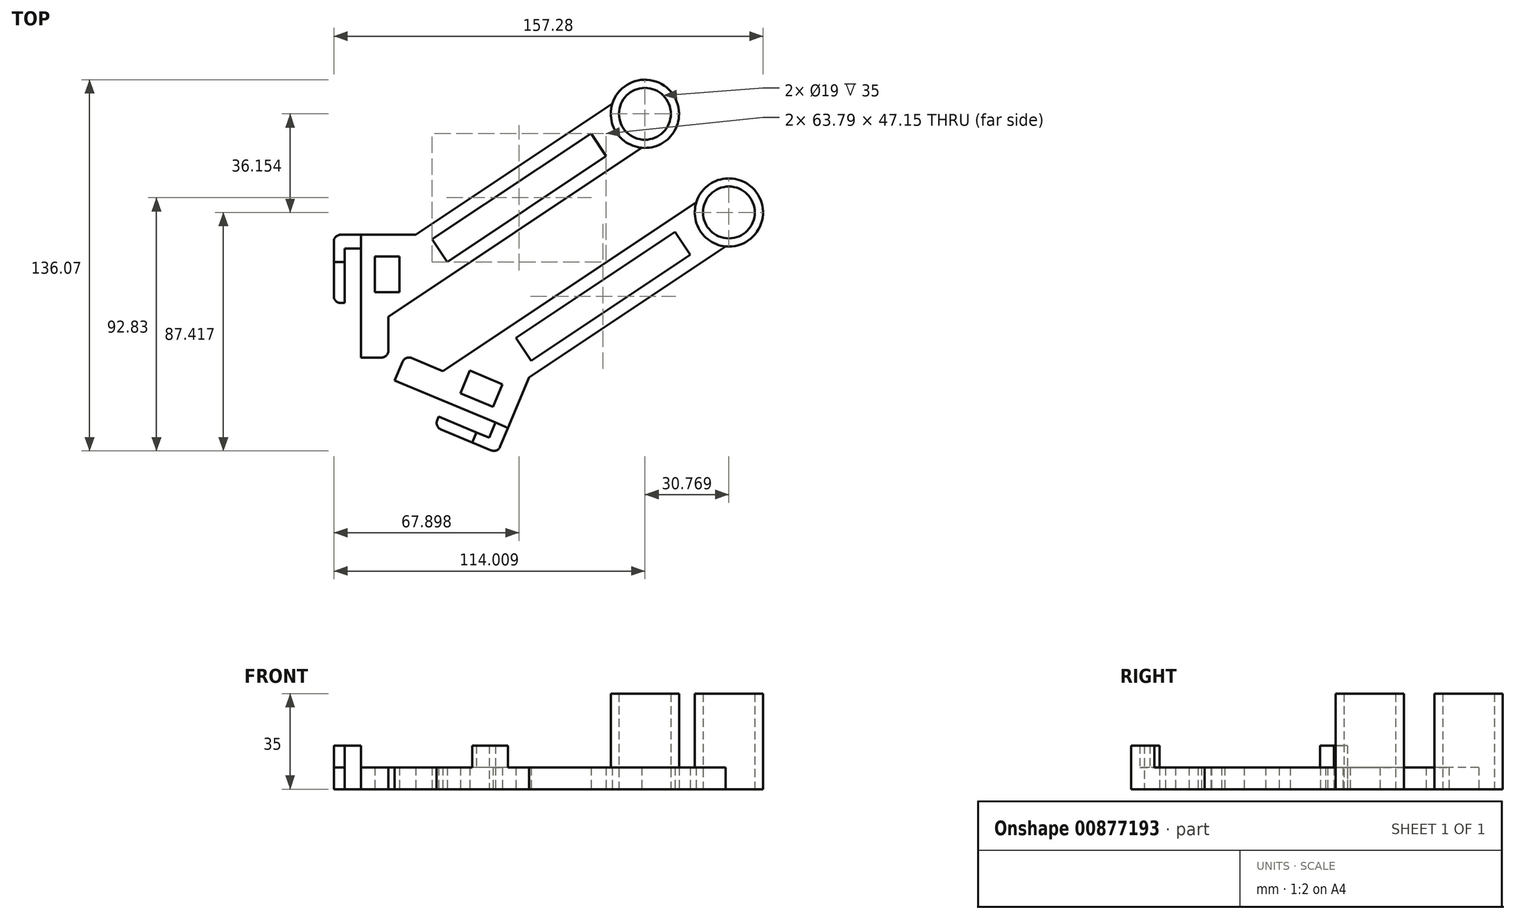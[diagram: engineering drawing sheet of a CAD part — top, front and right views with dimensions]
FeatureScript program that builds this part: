
annotation { "Feature Type Name" : "Feature", "Feature Type Description" : "" }
export const myFeature = defineFeature(function(context is Context, id is Id, definition is map)
    precondition{}
    {
        {
            var Q0;
            Q0=qCreatedBy(makeId("Top.planeOp"),FACE);
            var sketch = newSketch(context, id + "F0", { "sketchPlane" : qUnion([Q0])});
            skLineSegment(sketch, "E0", {"start": v(-44.07, 16.95) * mm, "end": v(-44.07, 36.95) * mm});
            skLineSegment(sketch, "E1", {"start": v(-44.07, 36.95) * mm, "end": v(-38.07, 36.95) * mm});
            skLineSegment(sketch, "E2", {"start": v(-38.07, 36.95) * mm, "end": v(-38.07, -3.05) * mm});
            skLineSegment(sketch, "E3", {"start": v(-38.07, -3.05) * mm, "end": v(-28.07, -3.05) * mm});
            skLineSegment(sketch, "E4", {"start": v(-28.07, -3.05) * mm, "end": v(-28.07, 11.95) * mm});
            skLineSegment(sketch, "E5", {"start": v(-28.07, 11.95) * mm, "end": v(64.77, 73.85) * mm});
            skLineSegment(sketch, "E6", {"start": v(54, 90) * mm, "end": v(-18.07, 41.95) * mm});
            skLineSegment(sketch, "E7", {"start": v(-18.07, 41.95) * mm, "end": v(-48.07, 41.95) * mm});
            skLineSegment(sketch, "E8", {"start": v(-48.07, 41.95) * mm, "end": v(-48.07, 16.95) * mm});
            skLineSegment(sketch, "E9", {"start": v(-48.07, 16.95) * mm, "end": v(-44.07, 16.95) * mm});
            skLineSegment(sketch, "E10.bottom", {"start": v(-33.07, 33.95) * mm, "end": v(-24.07, 33.95) * mm});
            skLineSegment(sketch, "E10.top", {"start": v(-33.07, 20.95) * mm, "end": v(-24.07, 20.95) * mm});
            skLineSegment(sketch, "E10.left", {"start": v(-33.07, 33.95) * mm, "end": v(-33.07, 20.95) * mm});
            skLineSegment(sketch, "E10.right", {"start": v(-24.07, 33.95) * mm, "end": v(-24.07, 20.95) * mm});
            skCircle(sketch, "E11", {"center": v(65.94, 86.3) * mm, "radius": 9.5 * mm});
            skLineSegment(sketch, "E12", {"start": v(65.94, 86.3) * mm, "end": v(-38.07, 16.95) * mm, "construction": true});
            skLineSegment(sketch, "E13", {"start": v(18.35, 42.9) * mm, "end": v(7.58, 59.05) * mm, "construction": true});
            skPoint(sketch, "E14", {"position": v(12.97, 50.98) * mm});
            skLineSegment(sketch, "E15", {"start": v(-12.07, 40.3) * mm, "end": v(-6.52, 31.98) * mm});
            skLineSegment(sketch, "E16", {"start": v(-6.52, 31.98) * mm, "end": v(51.72, 70.8) * mm});
            skLineSegment(sketch, "E17", {"start": v(51.72, 70.8) * mm, "end": v(46.18, 79.13) * mm});
            skLineSegment(sketch, "E18", {"start": v(46.18, 79.13) * mm, "end": v(-12.07, 40.3) * mm});
            skPoint(sketch, "E19", {"position": v(-9.3, 36.14) * mm});
            skCircle(sketch, "E20.0", {"center": v(65.94, 86.3) * mm, "radius": 12.5 * mm});
            skLineSegment(sketch, "E21", {"start": v(-48.07, 31.95) * mm, "end": v(-44.07, 31.95) * mm});
            skLineSegment(sketch, "E22", {"start": v(-38.07, 36.95) * mm, "end": v(-38.07, 41.95) * mm});
            skSolve(sketch);
        }
        {
            var Q0;
            Q0=qSketchRegion(id+"F0",true);
            extrude(context, id + "F1", {"entities" : qUnion([Q0]), "depth" : 8 * mm});
        }
        {
            var Q0;
            Q0=makeQuery(id+"F0.imprint","IMPRINT",FACE,{"disambiguationData":[TD([[makeQuery(id+"F0.imprint","IMPRINT",EDGE,{"derivedFrom":sQuery(id+"F0.wireOp",EDGE,"E11")}),-1.0]])]});
            extrude(context, id + "F2", {"entities" : qUnion([Q0]), "operationType" : NewBodyOperationType.ADD, "depth" : 35 * mm});
        }
        {
            var Q0;
            {var subQ5=sQuery(id+"F0.wireOp",EDGE,"E1");Q0=makeQuery(id+"F0.imprint","IMPRINT",FACE,{"disambiguationData":[TD([[makeQuery(id+"F0.imprint","IMPRINT",EDGE,{"derivedFrom":subQ5}),1.0]])]});}
            extrude(context, id + "F3", {"entities" : qUnion([Q0]), "operationType" : NewBodyOperationType.ADD, "depth" : 16 * mm});
        }
        {
            var Q0;
            Q0=makeQuery(id+"F1.opExtrude","SWEPT_EDGE",EDGE,{"disambiguationData":[OSD([sQuery(id+"F0.wireOp",EDGE,"E3"),sQuery(id+"F0.wireOp",EDGE,"E4")])]});
            var Q1;
            Q1=makeQuery(id+"F1.opExtrude","SWEPT_EDGE",EDGE,{"disambiguationData":[OSD([sQuery(id+"F0.wireOp",EDGE,"E8"),sQuery(id+"F0.wireOp",EDGE,"E9")])]});
            var Q2;
            {var subQ0=sQuery(id+"F0.wireOp",EDGE,"E8");var subQ1=sQuery(id+"F0.wireOp",EDGE,"E7");Q2=makeQuery(id+"F3.boolean.opBoolean","MERGE",EDGE,{"derivedFrom":[makeQuery(id+"F1.opExtrude","SWEPT_EDGE",EDGE,{"disambiguationData":[OSD([subQ1,subQ0])]}),makeQuery(id+"F3.opExtrude","SWEPT_EDGE",EDGE,{"disambiguationData":[OSD([subQ1,subQ0])]})]});}
            fillet(context, id + "F4", {"entities" : qUnion([Q0, Q1, Q2]), "radius" : 2.5 * mm, "tangentPropagation" : true, "allowEdgeOverflow" : false});
        }
        {
            var Q0;
            Q0=makeQuery(id+"F1.opExtrude","SWEPT_BODY",BODY,{"disambiguationData":[OSD([sQuery(id+"F0.wireOp",EDGE,"E0"),sQuery(id+"F0.wireOp",EDGE,"E1"),sQuery(id+"F0.wireOp",EDGE,"E2"),sQuery(id+"F0.wireOp",EDGE,"E3"),sQuery(id+"F0.wireOp",EDGE,"E4"),sQuery(id+"F0.wireOp",EDGE,"E5"),sQuery(id+"F0.wireOp",EDGE,"E6"),sQuery(id+"F0.wireOp",EDGE,"E7"),sQuery(id+"F0.wireOp",EDGE,"E8"),sQuery(id+"F0.wireOp",EDGE,"E9"),sQuery(id+"F0.wireOp",EDGE,"E10.bottom"),sQuery(id+"F0.wireOp",EDGE,"E10.top"),sQuery(id+"F0.wireOp",EDGE,"E10.left"),sQuery(id+"F0.wireOp",EDGE,"E10.right"),sQuery(id+"F0.wireOp",EDGE,"E11"),sQuery(id+"F0.wireOp",EDGE,"E15"),sQuery(id+"F0.wireOp",EDGE,"E16"),sQuery(id+"F0.wireOp",EDGE,"E17"),sQuery(id+"F0.wireOp",EDGE,"E18"),sQuery(id+"F0.wireOp",EDGE,"E20.0")])]});
            var Q1;
            Q1=makeQuery(id+"F1.opExtrude","SWEPT_FACE",FACE,{"disambiguationData":[OSD([sQuery(id+"F0.wireOp",EDGE,"E5")])]});
            mirror(context, id + "F5", {"entities" : qUnion([Q0]), "mirrorPlane" : qUnion([Q1])});
        }
        {
            var Q0;
            Q0=makeQuery(id+"F5.opPattern","COPY",BODY,{"derivedFrom":makeQuery(id+"F1.opExtrude","SWEPT_BODY",BODY,{"disambiguationData":[OSD([sQuery(id+"F0.wireOp",EDGE,"E0"),sQuery(id+"F0.wireOp",EDGE,"E1"),sQuery(id+"F0.wireOp",EDGE,"E2"),sQuery(id+"F0.wireOp",EDGE,"E3"),sQuery(id+"F0.wireOp",EDGE,"E4"),sQuery(id+"F0.wireOp",EDGE,"E5"),sQuery(id+"F0.wireOp",EDGE,"E6"),sQuery(id+"F0.wireOp",EDGE,"E7"),sQuery(id+"F0.wireOp",EDGE,"E8"),sQuery(id+"F0.wireOp",EDGE,"E9"),sQuery(id+"F0.wireOp",EDGE,"E10.bottom"),sQuery(id+"F0.wireOp",EDGE,"E10.top"),sQuery(id+"F0.wireOp",EDGE,"E10.left"),sQuery(id+"F0.wireOp",EDGE,"E10.right"),sQuery(id+"F0.wireOp",EDGE,"E11"),sQuery(id+"F0.wireOp",EDGE,"E15"),sQuery(id+"F0.wireOp",EDGE,"E16"),sQuery(id+"F0.wireOp",EDGE,"E17"),sQuery(id+"F0.wireOp",EDGE,"E18"),sQuery(id+"F0.wireOp",EDGE,"E20.0")])]}),"instanceName":"1"});
            transform(context, id + "F6", {"entities" : qUnion([Q0]), "transformType" : TransformType.TRANSLATION_3D, "dx" : 20 * mm, "dy" : -20 * mm, "dz" : 0 * mm, "makeCopy" : false});
        }
    });
